FCSTD DOCUMENT  (FreeCAD 0.19RUnknown)
Label: 3D printer size
License: All rights reserved
LicenseURL: http://en.wikipedia.org/wiki/All_rights_reserved
objects: Sketcher::SketchObject×1
note: 1 computed .brp shape members not serialized (recipe doc carries the construction recipe); baked Part::Feature solids carry a one-line shape summary decoded from their .brp

FEATURE [Sketcher::SketchObject] Sketch
  FullyConstrained = true
  sketch-geometry (8):
    g0: LineSegment StartX=0 StartY=296.985 StartZ=0 EndX=296.985 EndY=296.985 EndZ=0
    g1: LineSegment StartX=296.985 StartY=296.985 StartZ=0 EndX=296.985 EndY=0 EndZ=0
    g2: LineSegment StartX=296.985 StartY=0 StartZ=0 EndX=0 EndY=0 EndZ=0
    g3: LineSegment StartX=0 StartY=0 StartZ=0 EndX=0 EndY=296.985 EndZ=0
    g4: LineSegment StartX=0 StartY=215.668 StartZ=0 EndX=81.3173 EndY=296.985 EndZ=0
    g5: LineSegment StartX=81.3173 StartY=296.985 StartZ=0 EndX=296.985 EndY=81.3173 EndZ=0
    g6: LineSegment StartX=296.985 StartY=81.3173 StartZ=0 EndX=215.668 EndY=0 EndZ=0
    g7: LineSegment StartX=215.668 StartY=0 StartZ=0 EndX=0 EndY=215.668 EndZ=0
  constraints (23):
    c: Coincident(g0,g1)
    c: Coincident(g1,g2)
    c: Coincident(g2,g3)
    c: Coincident(g3,g0)
    c: Horizontal(g0)
    c: Horizontal(g2)
    c: Vertical(g1)
    c: Vertical(g3)
    c: PointOnObject(g4,g3)
    c: PointOnObject(g4,g0)
    c: Coincident(g4,g5)
    c: PointOnObject(g5,g1)
    c: Coincident(g5,g6)
    c: PointOnObject(g6,g2)
    c: Coincident(g6,g7)
    c: Coincident(g7,g4)
    c: Parallel(g4,g6)
    c: Parallel(g5,g7)
    c: Angle(g7,g4) = 1.5708
    c: Distance(g4) = 115
    c: Distance(g5) = 305
    c: Angle(g7,g2) = 0.785398
    c: Coincident(g2,g-1)
